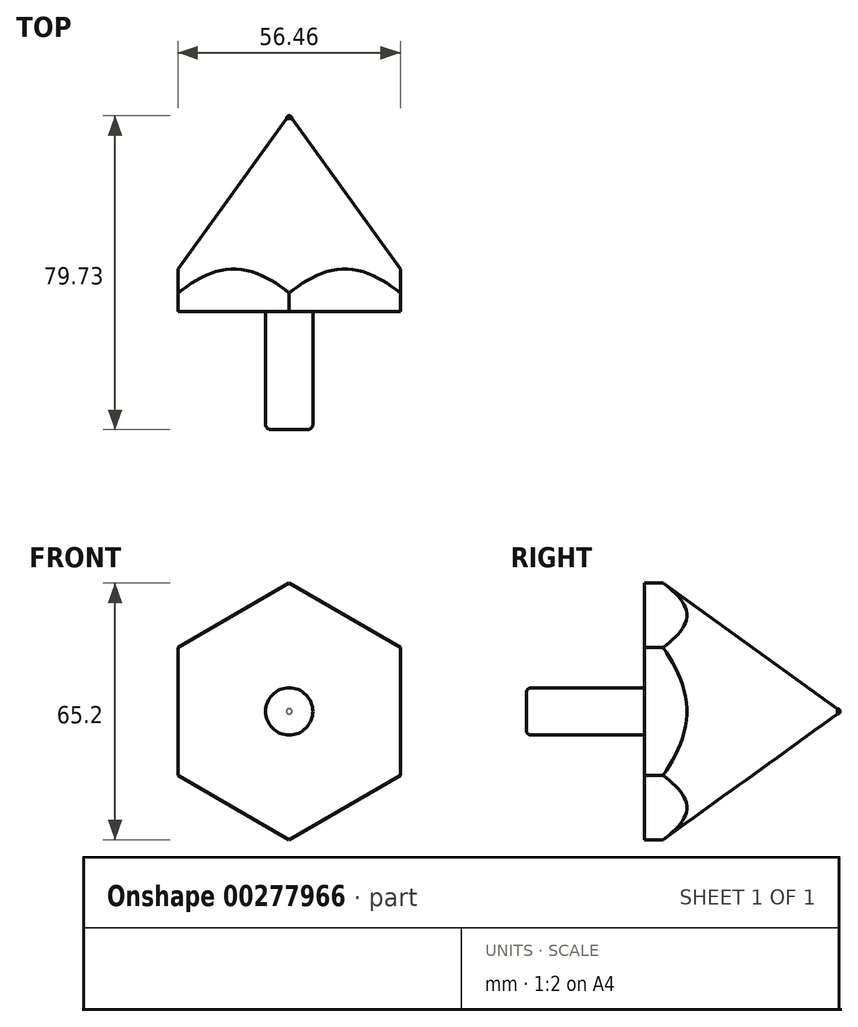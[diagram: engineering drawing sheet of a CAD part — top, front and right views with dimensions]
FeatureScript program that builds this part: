
annotation { "Feature Type Name" : "Feature", "Feature Type Description" : "" }
export const myFeature = defineFeature(function(context is Context, id is Id, definition is map)
    precondition{}
    {
        {
            var Q0;
            Q0=qCreatedBy(makeId("Right.planeOp"),FACE);
            var sketch = newSketch(context, id + "F0", { "sketchPlane" : qUnion([Q0])});
            skLineSegment(sketch, "E0", {"start": v(0, 0) * mm, "end": v(35.47, 0) * mm, "construction": true});
            skLineSegment(sketch, "E1", {"start": v(0, 0) * mm, "end": v(0, 4.73) * mm});
            skLineSegment(sketch, "E2", {"start": v(1.27, 6) * mm, "end": v(30, 6) * mm});
            skLineSegment(sketch, "E3", {"start": v(30, 6) * mm, "end": v(30, 33.52) * mm});
            skLineSegment(sketch, "E4", {"start": v(32.01, 34.55) * mm, "end": v(79.04, 0.7) * mm});
            skLineSegment(sketch, "E5", {"start": v(79.73, 0) * mm, "end": v(0, 0) * mm});
            skLineSegment(sketch, "E6", {"start": v(0, 0) * mm, "end": v(79.73, 0) * mm, "construction": true});
            skPoint(sketch, "E7.visualSharp", {"position": v(0, 6) * mm});
            skArc(sketch, "E7.filletArc", {"start": v(1.27, 6) * mm, "mid": v(0.37, 5.63) * mm, "end": v(0, 4.73) * mm});
            skPoint(sketch, "E8.visualSharp", {"position": v(30, 36) * mm});
            skArc(sketch, "E8.filletArc", {"start": v(32.01, 34.55) * mm, "mid": v(30.7, 34.65) * mm, "end": v(30, 33.52) * mm});
            skLineSegment(sketch, "E9", {"start": v(79.04, 0) * mm, "end": v(79.04, 0.7) * mm, "construction": true});
            skArc(sketch, "E10", {"start": v(79.04, 0.7) * mm, "mid": v(79.53, 0.49) * mm, "end": v(79.73, 0) * mm});
            skPoint(sketch, "E11.orphan", {"position": v(80, 0) * mm});
            skLineSegment(sketch, "E12.trimOffspring", {"start": v(80, 0) * mm, "end": v(104.38, 0) * mm, "construction": true});
            skSolve(sketch);
        }
        {
            var Q0;
            Q0 = qSketchRegion(id + "F0", true);
            var Q1;
            Q1=sQuery(id+"F0.wireOp",EDGE,"E12.trimOffspring");
            revolve(context, id + "F1", {"entities" : qUnion([Q0]), "axis" : qUnion([Q1]), "revolveType" : RevolveType.FULL});
        }
        {
            var Q0;
            Q0=makeQuery(id+"F1.opRevolve","SWEPT_FACE",FACE,{"disambiguationData":[OSD([sQuery(id+"F0.wireOp",EDGE,"E3")])]});
            var sketch = newSketch(context, id + "F2", { "sketchPlane" : qUnion([Q0])});
            skSolve(sketch);
        }
        {
            var Q0;
            {var subQ0=sQuery(id+"F0.wireOp",EDGE,"E3");Q0=makeQuery(id+"F2.imprint","IMPRINT",FACE,{"disambiguationData":[TD([[makeQuery(id+"F2.imprint","IMPRINT",EDGE,{"derivedFrom":makeQuery(id+"F1.opRevolve","SWEPT_EDGE",EDGE,{"disambiguationData":[OSD([sQuery(id+"F0.wireOp",EDGE,"E2"),subQ0])]})}),-1.0]])]});}
            var sketch = newSketch(context, id + "F3", { "sketchPlane" : qUnion([Q0])});
            skCircle(sketch, "E13", {"center": v(0, 0) * mm, "radius": 42.2 * mm});
            skCircle(sketch, "E14.cCircle", {"center": v(0, 0) * mm, "radius": 28.23 * mm, "construction": true});
            skLineSegment(sketch, "E14.0", {"start": v(28.23, 16.3) * mm, "end": v(28.23, -16.3) * mm});
            skLineSegment(sketch, "E14.1", {"start": v(28.23, -16.3) * mm, "end": v(0, -32.6) * mm});
            skLineSegment(sketch, "E14.2", {"start": v(0, -32.6) * mm, "end": v(-28.23, -16.3) * mm});
            skLineSegment(sketch, "E14.3", {"start": v(-28.23, -16.3) * mm, "end": v(-28.23, 16.3) * mm});
            skLineSegment(sketch, "E14.4", {"start": v(-28.23, 16.3) * mm, "end": v(0, 32.6) * mm});
            skLineSegment(sketch, "E14.5", {"start": v(0, 32.6) * mm, "end": v(28.23, 16.3) * mm});
            skPoint(sketch, "E14.0.midPoint", {"position": v(28.23, 0) * mm});
            skSolve(sketch);
        }
        {
            var Q0;
            Q0 = qSketchRegion(id + "F3", true);
            extrude(context, id + "F4", {"entities" : qUnion([Q0]), "operationType" : NewBodyOperationType.REMOVE, "oppositeDirection" : true, "depth" : 25.4 * mm});
        }
    });
